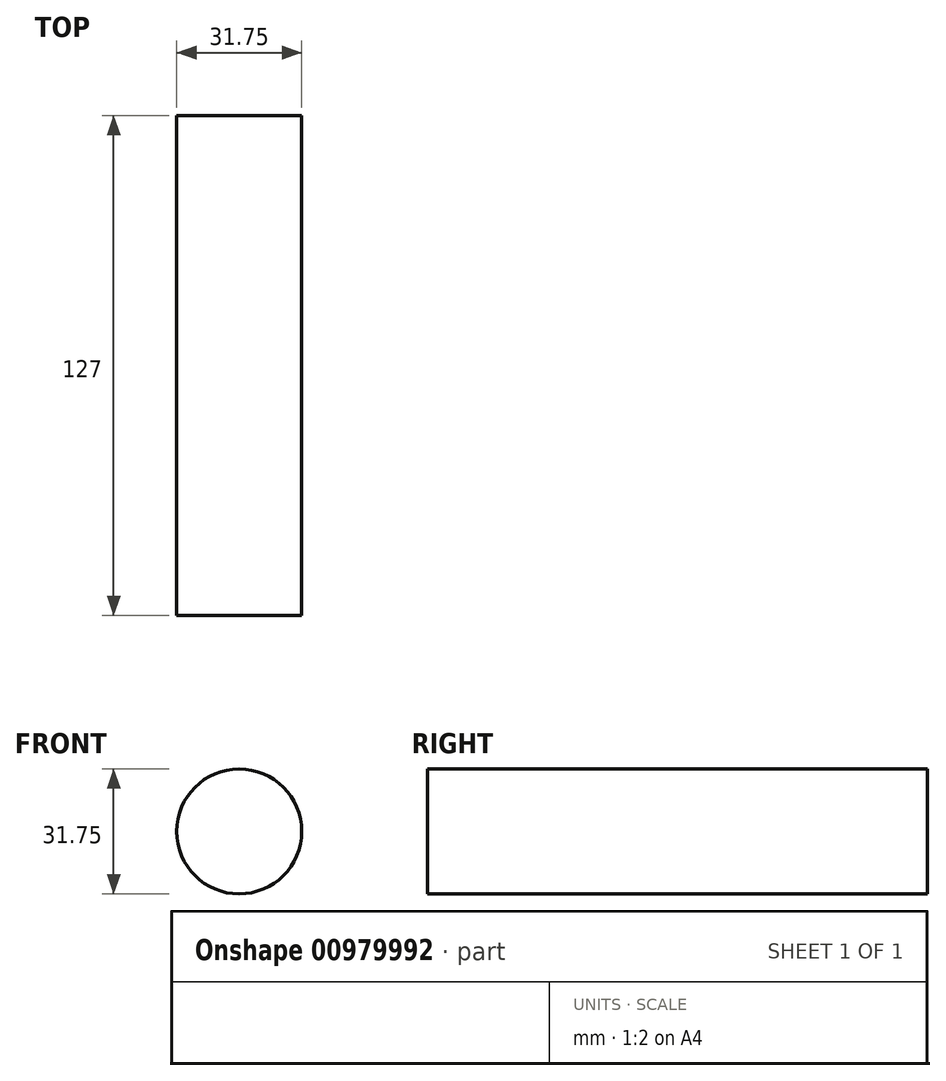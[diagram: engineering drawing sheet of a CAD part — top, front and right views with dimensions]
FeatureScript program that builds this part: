
annotation { "Feature Type Name" : "Feature", "Feature Type Description" : "" }
export const myFeature = defineFeature(function(context is Context, id is Id, definition is map)
    precondition{}
    {
        {
            var Q0;
            Q0=qCreatedBy(makeId("Front.planeOp"),FACE);
            var sketch = newSketch(context, id + "F0", { "sketchPlane" : qUnion([Q0])});
            skCircle(sketch, "E0", {"center": v(-67.1, 2.89) * mm, "radius": 15.88 * mm});
            skSolve(sketch);
        }
        {
            var Q0;
            Q0=makeQuery(id+"F0.imprint","IMPRINT",FACE,{"disambiguationData":[TD([[makeQuery(id+"F0.imprint","IMPRINT",EDGE,{"derivedFrom":sQuery(id+"F0.wireOp",EDGE,"E0")}),1.0]])]});
            extrude(context, id + "F1", {"entities" : qUnion([Q0]), "depth" : 127 * mm, "offsetDistance" : 25.4 * mm});
        }
    });
